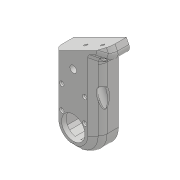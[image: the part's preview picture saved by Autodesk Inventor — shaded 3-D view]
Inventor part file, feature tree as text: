
AUTODESK INVENTOR PART (.ipt)
format: ipt  version: 2018 (Build 220112000, 112)  size: 929,792 bytes
history: native  units: mm
features: sketch x31, projected_geometry x26, extrude x24, hole x10, fillet x10, chamfer x3, mirror x1, plane x1
ambient origin geometry x8: Origin, YZ Plane, XZ Plane, XY Plane, X Axis, Y Axis, Z Axis, Center Point
bodies: Solid1 (feature_tree)
feature tree (106):
  extrude  "Extrusion1"  Depth=45.0mm
  extrude  "Extrusion2"  Depth=2.25mm
  hole  "Hole1"  [1 undecoded]
  hole  "Hole2"  [1 undecoded]
  fillet  "Fillet1"  Radius=14.0mm
  extrude  "Extrusion3"  Depth=18.5mm
  extrude  "Extrusion4"  Depth=10.0mm
  extrude  "Extrusion5"  Depth=2.195mm
  extrude  "Extrusion6"  Depth=20.5mm
  hole  "Hole3"  [1 undecoded]
  extrude  "Extrusion7"  Depth=0.5mm
  extrude  "Extrusion8"  Depth=5.0mm TaperAngle=0.0deg
  extrude  "Extrusion9"  Depth=10.0mm
  extrude  "Extrusion10"  Depth=10.0mm
  extrude  "Extrusion11"  Depth=14.5mm
  extrude  "Extrusion12"  Depth=14.5mm
  extrude  "Extrusion13"  Depth=5.0mm
  extrude  "Extrusion14"  Depth=5.0mm
  extrude  "Extrusion15"  Depth=5.0mm
  extrude  "Extrusion16"  Depth=5.0mm
  extrude  "Extrusion17"  Depth=4.0mm
  chamfer  "Chamfer1"  Distance=1.0mm
  fillet  "Fillet7"  Radius=20.7mm
  fillet  "Fillet8"  Radius=32.0mm
  mirror  "Mirror1"
  extrude  "Extrusion24"  Depth=5.0mm TaperAngle=0.0deg
  extrude  "Extrusion25"  Depth=8.0mm
  extrude  "Extrusion26"  Depth=0.2mm TaperAngle=0.0deg
  extrude  "Extrusion27"  Depth=0.5mm TaperAngle=0.0deg
  extrude  "Extrusion28"  Depth=5.0mm TaperAngle=0.0deg
  chamfer  "Chamfer5"  Distance=5.0mm
  fillet  "Fillet18"  Radius=0.2mm
  fillet  "Fillet19"  Radius=0.2mm
  extrude  "Extrusion29"  Depth=1.5mm
  chamfer  "Chamfer6"  Distance=70.0mm
  hole  "Hole10"  [1 undecoded]
  plane  "Work Plane2"
  hole  "Hole11"  [1 undecoded]
  fillet  "Fillet20"  Radius=10.0mm
  sketch  "Sketch43"  dims[d102=2.5mm d103=2.0mm d104=45.0deg d105=1.5mm]
  hole  "Hole12"  [1 undecoded]
  hole  "Hole13"  [1 undecoded]
  hole  "Hole14"  [1 undecoded]
  fillet  "Fillet21"  Radius=10.0mm
  fillet  "Fillet22"  Radius=2.0mm
  hole  "Hole15"  [1 undecoded]
  fillet  "Fillet23"  Radius=5.0mm
  hole  "Hole16"  [1 undecoded]
  fillet  "Fillet24"  Radius=15.0mm
  extrude  "Extrusion30"  Depth=1.5mm TaperAngle=0.0deg
  sketch  "Sketch1"  dims[d0=24.5mm d1=45.0mm]
  sketch  "Sketch2"  dims[d2=1.95mm d3=0.0mm d4=2.25mm]
  projected_geometry  "Projected Loop1"
  sketch  "Sketch3"  dims[d5=20.0mm d6=2.25mm]
  projected_geometry  "Projected Loop2"
  sketch  "Sketch4"  dims[d7=5.25mm d8=5.25mm d9=14.0mm]
  projected_geometry  "Projected Loop3"
  sketch  "Sketch5"  dims[d10=5.25mm d11=18.5mm]
  projected_geometry  "Projected Loop4"
  sketch  "Sketch6"  dims[d12=10.0mm d13=0.0mm d14=20.5mm]
  projected_geometry  "Projected Loop5"
  sketch  "Sketch7"  dims[d15=2.0mm d16=2.195mm]
  projected_geometry  "Projected Loop6"
  sketch  "Sketch8"  dims[d17=2.0mm]
  projected_geometry  "Projected Loop7"
  sketch  "Sketch9"  dims[d18=2.4mm d19=6.0mm d20=4.4mm d21=2.0mm d22=90.0deg d23=8.0mm d24=20.594885mm d25=20.5mm]
  projected_geometry  "Projected Loop8"
  projected_geometry  "Projected Loop9"
  sketch  "Sketch10"  dims[d26=26.65mm d27=2.0mm]
  projected_geometry  "Projected Loop10"
  projected_geometry  "Projected Loop11"
  sketch  "Sketch11"  dims[d28=2.0mm]
  projected_geometry  "Projected Loop12"
  sketch  "Sketch12"  dims[d29=2.4mm d30=6.0mm d31=4.4mm d32=2.0mm d33=90.0deg d34=8.0mm d35=20.594885mm d36=0.5mm]
  sketch  "Sketch13"  dims[d37=18.0mm d38=5.0mm d39=0.0mm]
  sketch  "Sketch14"  dims[d41=10.0mm d42=0.0mm d43=24.5mm]
  projected_geometry  "Projected Loop13"
  sketch  "Sketch15"  dims[d44=1.15mm d45=0.0mm d46=10.0mm]
  sketch  "Sketch16"  dims[d47=21.0mm d48=14.5mm]
  projected_geometry  "Projected Loop14"
  sketch  "Sketch17"  dims[d49=20.0mm d50=14.5mm]
  projected_geometry  "Projected Loop15"
  sketch  "Sketch18"  dims[d51=24.5mm d52=5.0mm]
  projected_geometry  "Projected Loop16"
  sketch  "Sketch19"  dims[d53=5.0mm d54=2.25mm]
  projected_geometry  "Projected Loop17"
  sketch  "Sketch20"  dims[d55=2.25mm d56=5.0mm]
  projected_geometry  "Projected Loop18"
  sketch  "Sketch35"  dims[d57=5.0mm d58=9.0mm]
  projected_geometry  "Projected Loop28"
  sketch  "Sketch36"  dims[d59=14.75mm d60=4.0mm d61=1.0mm d62=0.0mm d63=20.7mm]
  projected_geometry  "Projected Loop29"
  sketch  "Sketch37"  dims[d64=2.4mm d65=6.0mm d66=4.4mm d67=2.0mm d68=90.0deg d69=8.0mm d70=20.594885mm d72=32.0mm]
  sketch  "Sketch38"  dims[d73=5.0mm d74=0.0mm d75=1.0mm d76=0.0mm]
  sketch  "Sketch39"  dims[d77=12.25mm d78=0.0mm d80=8.0mm]
  projected_geometry  "Projected Loop30"
  sketch  "Sketch40"  dims[d81=4.5mm d82=0.0mm d84=0.2mm d85=0.0mm]
  projected_geometry  "Projected Loop31"
  sketch  "Sketch41"  dims[d86=21.0mm d87=0.5mm d88=0.0mm]
  projected_geometry  "Projected Loop32"
  projected_geometry  "Projected Loop33"
  sketch  "Sketch42"  dims[d91=8.0mm d92=0.0mm d93=5.0mm d94=0.0mm d95=5.0mm d96=0.0mm d98=0.2mm d99=0.0mm d100=0.2mm d101=0.0mm]
  projected_geometry  "Projected Loop34"
  sketch  "Sketch44"  dims[d114=0.5mm]
  projected_geometry  "Projected Loop35"
  sketch  "Sketch45"  dims[d187=40.0mm d188=70.0mm d189=20.0mm d190=10.0mm d191=0.0mm d192=10.0mm d193=0.0mm d194=2.0mm d195=0.0mm d196=2.0mm d197=0.0mm d198=8.0mm d199=10.0mm d200=2.0mm d201=0.0mm d204=7.0mm d205=2.0mm d206=45.0deg d207=5.0mm d208=8.0mm d209=15.0mm d210=2.0mm d211=0.0mm d212=1.5mm d213=2.0mm d214=45.0deg d215=24.0mm d216=17.0mm d217=3.5mm d218=3.2mm d219=6.0mm d220=9.4mm d221=2.0mm d222=90.0deg d223=8.0mm d224=20.594885mm d225=6.0mm d226=6.0mm d227=9.4mm d228=2.0mm d229=90.0deg d230=69.0mm d231=0.0mm d232=1.0mm d233=8.0mm d234=2.459mm d235=6.0mm d236=9.4mm d237=2.0mm d238=90.0deg d239=34.0mm d240=20.594885mm d241=3.2mm d242=6.0mm d243=6.3mm d244=2.0mm d245=90.0deg d246=20.55mm d247=0.0mm d248=6.0mm d249=6.0mm d250=6.3mm d251=2.0mm d252=90.0deg d253=10.0mm d254=0.0mm d255=1.5mm d256=0.75mm d257=4.0mm d258=6.0mm d259=4.4mm d260=2.0mm d261=90.0deg d262=2.5mm d263=0.0mm d264=1.0mm d265=4.0mm d266=6.0mm d267=4.4mm d268=2.0mm d269=90.0deg d270=2.5mm d271=0.0mm d272=1.0mm d273=20.55mm d274=0.0mm]
note: 10 required parameter values undecoded (feature->parameter linkage not recoverable at this tier; creation-order binding heuristic only, values carry confidence <= 0.55)
